SOLIDWORKS PART (.sldprt)
format: sldprt  version: not decoded by parser v0  size: 171,008 bytes
history: native  units: mm
features: plane x4, sketch x3, fillet x3, extrude x2, material x1, cut_extrude x1, mirror x1 (+8 scaffold rows collapsed)
feature tree (23):
  scaffold x8  (default folders/planes/origin — collapsed)
  material  "Matériau <non spécifié>"
  plane  "Plan de face"
  plane  "Plan de dessus"
  plane  "Plan de droite"
  sketch  "Esquisse1"  dims[D1=20.0mm D2=20.0mm D3=20.0mm D4=20.0mm]
  extrude  "Boss.-Extru.1"  Depth=5mm
  sketch  "Esquisse2"  dims[D1=5.0mm D2=5.0mm D3=5.0mm D4=5.0mm]
  extrude  "Boss.-Extru.2"  Depth=20mm
  fillet  "Congé2"  Radius=2mm
  fillet  "Congé3"  Radius=2mm
  fillet  "Congé4"  Radius=2mm
  sketch  "Esquisse3"  dims[D1=10.0mm D2=60.0mm D3=6.0mm D4=9.0mm]
  cut_extrude  "Enlèv. mat.-Extru.1"  [1 undecoded]
  plane  "Plan1"
  mirror  "Symétrie1"
decode coverage: 8 of 10 modeling features carry decoded parameters
note: 1 parameter value undecoded
note: suppression state not decoded; provenance and decode notes live in map.json
